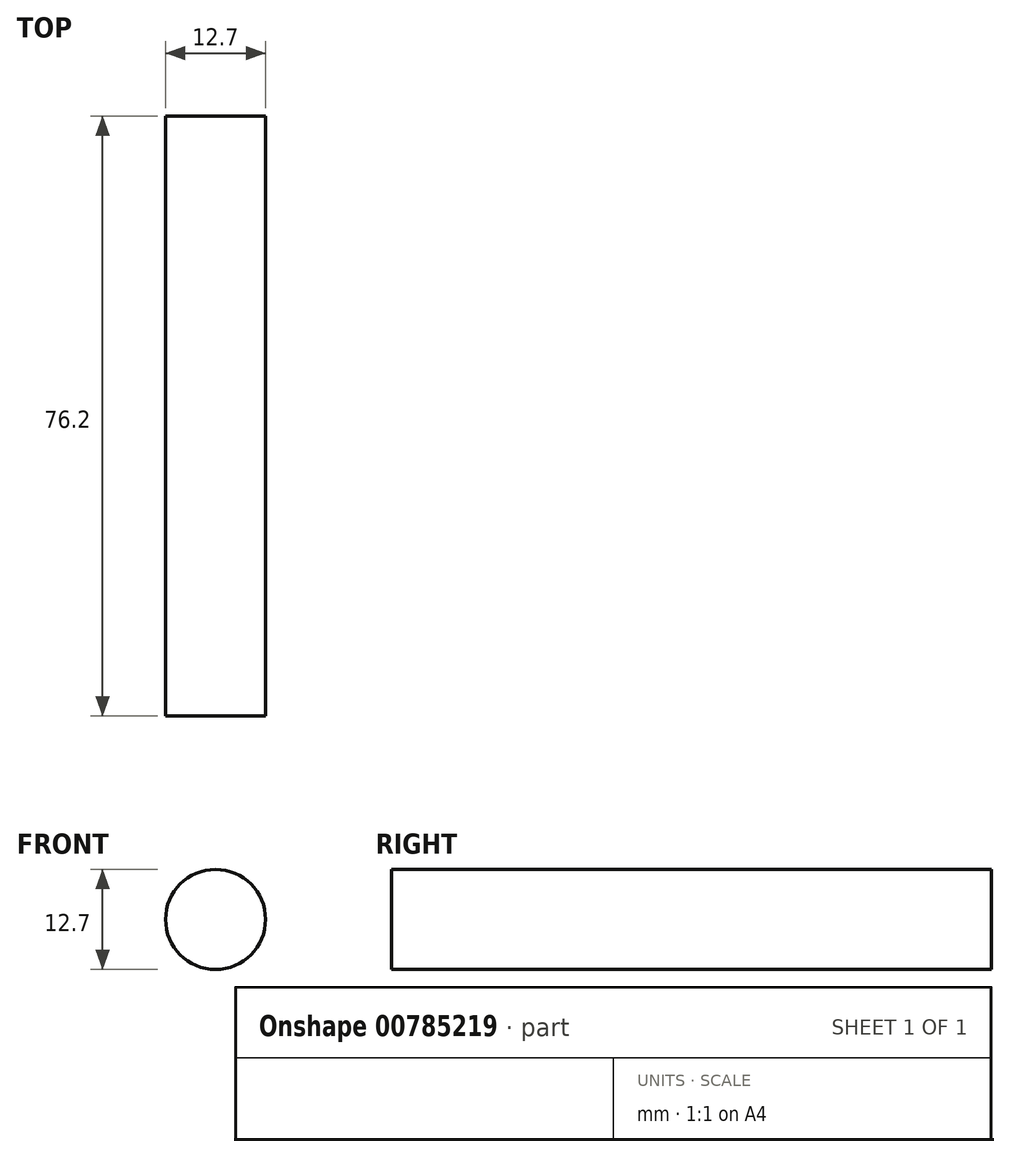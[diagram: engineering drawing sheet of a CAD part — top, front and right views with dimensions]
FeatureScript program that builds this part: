
annotation { "Feature Type Name" : "Feature", "Feature Type Description" : "" }
export const myFeature = defineFeature(function(context is Context, id is Id, definition is map)
    precondition{}
    {
        {
            var Q0;
            Q0=qCreatedBy(makeId("Front.planeOp"),FACE);
            var sketch = newSketch(context, id + "F0", { "sketchPlane" : qUnion([Q0])});
            skCircle(sketch, "E0", {"center": v(0, 0) * mm, "radius": 6.35 * mm});
            skSolve(sketch);
        }
        {
            var Q0;
            Q0=makeQuery(id+"F0.imprint","IMPRINT",FACE,{"disambiguationData":[TD([[makeQuery(id+"F0.imprint","IMPRINT",EDGE,{"derivedFrom":sQuery(id+"F0.wireOp",EDGE,"E0")}),1.0]])]});
            extrude(context, id + "F1", {"entities" : qUnion([Q0]), "depth" : 76.2 * mm, "offsetDistance" : 25.4 * mm});
        }
    });
